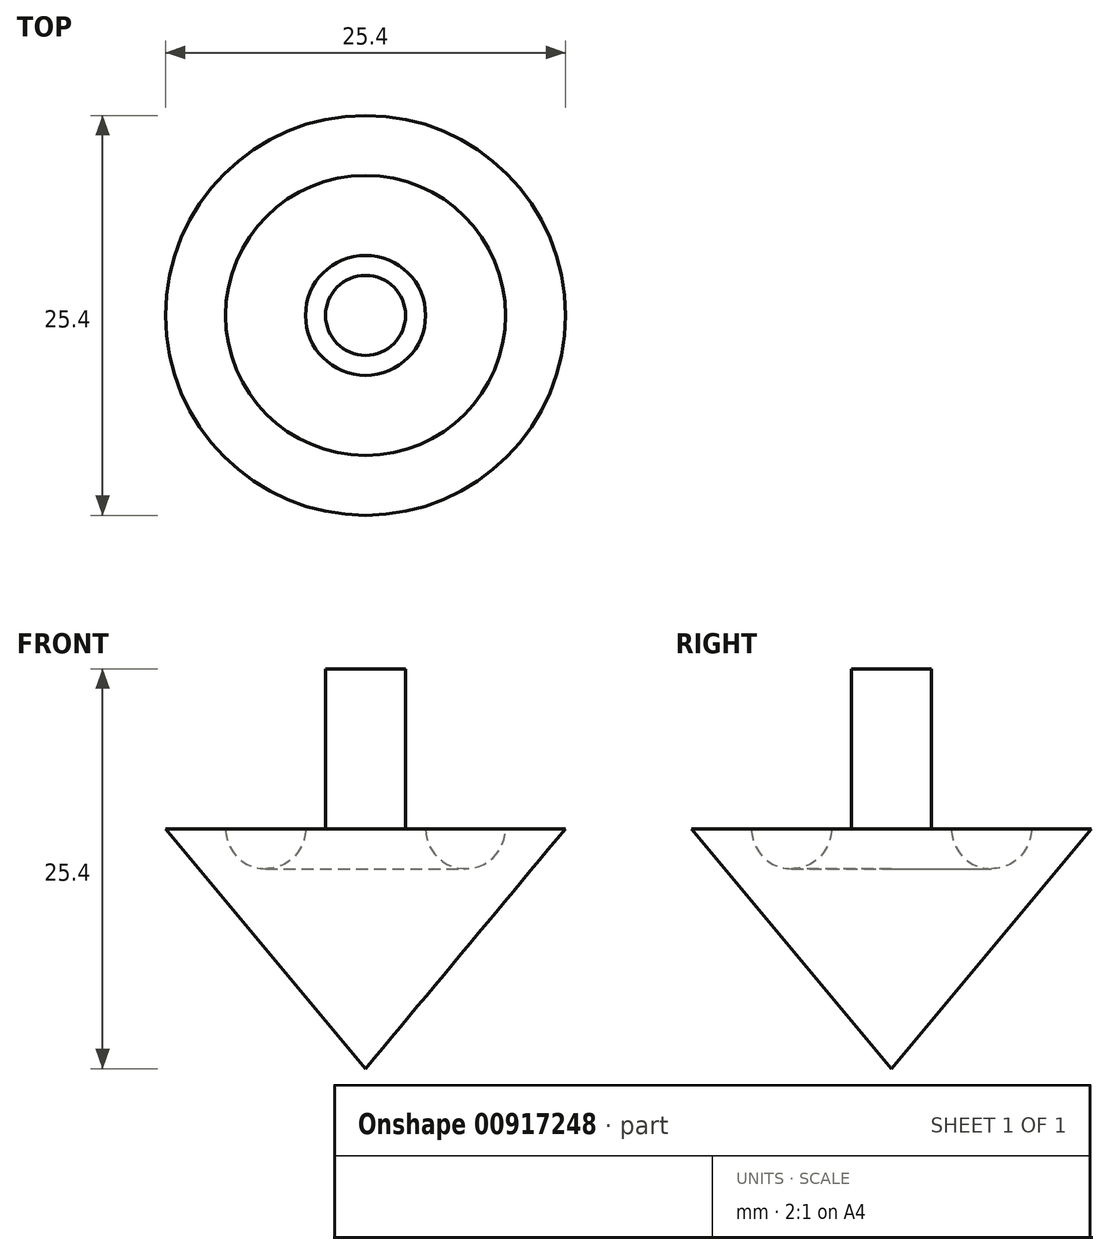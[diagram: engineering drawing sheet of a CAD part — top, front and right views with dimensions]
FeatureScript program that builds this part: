
annotation { "Feature Type Name" : "Feature", "Feature Type Description" : "" }
export const myFeature = defineFeature(function(context is Context, id is Id, definition is map)
    precondition{}
    {
        {
            var Q0;
            Q0=qCreatedBy(makeId("Front.planeOp"),FACE);
            var sketch = newSketch(context, id + "F0", { "sketchPlane" : qUnion([Q0])});
            skLineSegment(sketch, "E0", {"start": v(0, 0) * mm, "end": v(0, -15.24) * mm});
            skLineSegment(sketch, "E1", {"start": v(0, 0) * mm, "end": v(-12.7, 0) * mm});
            skLineSegment(sketch, "E2", {"start": v(-12.7, 0) * mm, "end": v(0, -15.24) * mm});
            skArc(sketch, "E3", {"start": v(-3.81, 0) * mm, "mid": v(-6.35, -2.54) * mm, "end": v(-8.9, 0) * mm});
            skSolve(sketch);
        }
        {
            var Q0;
            {var subQ3=sQuery(id+"F0.wireOp",EDGE,"E0");Q0=makeQuery(id+"F0.imprint","IMPRINT",FACE,{"disambiguationData":[TD([[makeQuery(id+"F0.imprint","IMPRINT",EDGE,{"derivedFrom":subQ3}),-1.0]])]});}
            var Q1;
            Q1=sQuery(id+"F0.wireOp",EDGE,"E0");
            revolve(context, id + "F1", {"surfaceOperationType" : NewSurfaceOperationType.NEW, "entities" : qUnion([Q0]), "axis" : qUnion([Q1]), "revolveType" : RevolveType.FULL});
        }
        {
            var Q0;
            {var subQ0=sQuery(id+"F0.wireOp",EDGE,"E1");Q0=makeQuery(id+"F1.opRevolve","SWEPT_FACE",FACE,{"disambiguationData":[OSD([subQ0]),TDD([makeQuery(id+"F0.imprint","IMPRINT",EDGE,{"disambiguationData":[TD([[makeQuery(id+"F0.imprint","INTERSECT",VERTEX,{"derivedFrom":[sQuery(id+"F0.wireOp",EDGE,"E0"),subQ0]}),-1.0]])],"derivedFrom":subQ0})])]});}
            var sketch = newSketch(context, id + "F2", { "sketchPlane" : qUnion([Q0])});
            skCircle(sketch, "E4", {"center": v(0, 0) * mm, "radius": 2.54 * mm});
            skSolve(sketch);
        }
        {
            var Q0;
            Q0=makeQuery(id+"F2.imprint","IMPRINT",FACE,{"disambiguationData":[TD([[makeQuery(id+"F2.imprint","IMPRINT",EDGE,{"derivedFrom":sQuery(id+"F2.wireOp",EDGE,"E4")}),1.0]])]});
            extrude(context, id + "F3", {"entities" : qUnion([Q0]), "operationType" : NewBodyOperationType.ADD, "depth" : 10.16 * mm, "offsetDistance" : 25.4 * mm});
        }
    });
